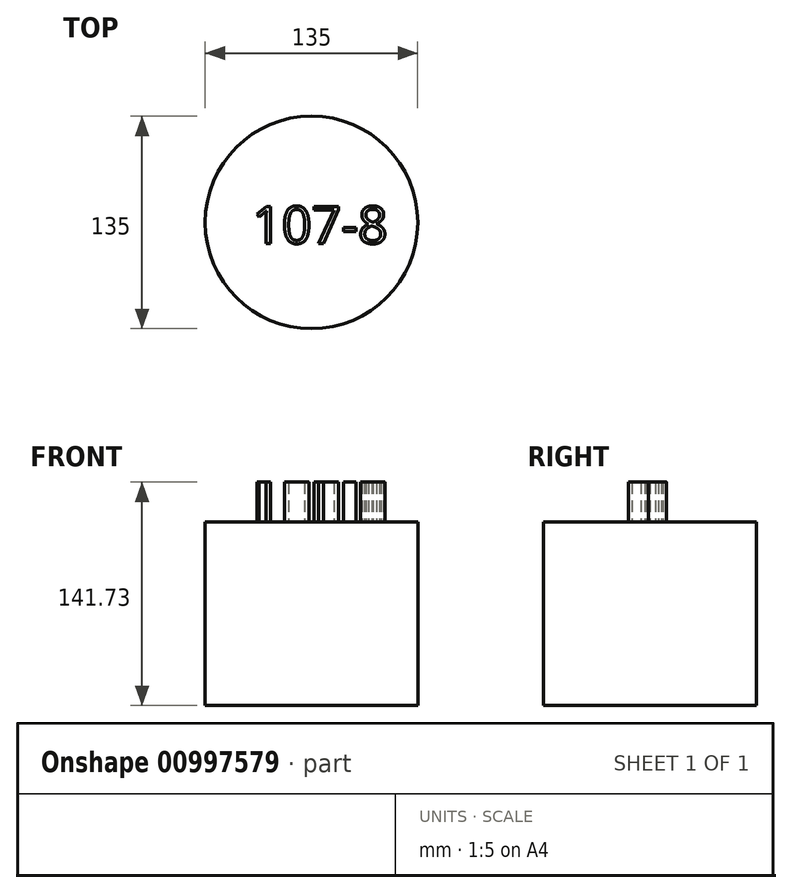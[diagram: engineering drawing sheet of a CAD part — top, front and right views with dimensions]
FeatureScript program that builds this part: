
annotation { "Feature Type Name" : "Feature", "Feature Type Description" : "" }
export const myFeature = defineFeature(function(context is Context, id is Id, definition is map)
    precondition{}
    {
        {
            var Q0;
            Q0=qCreatedBy(makeId("Top.planeOp"),FACE);
            var sketch = newSketch(context, id + "F0", { "sketchPlane" : qUnion([Q0])});
            skCircle(sketch, "E0", {"center": v(0, 0) * mm, "radius": 67.5 * mm});
            skSolve(sketch);
        }
        {
            var Q0;
            Q0=makeQuery(id+"F0.imprint","IMPRINT",FACE,{"disambiguationData":[TD([[makeQuery(id+"F0.imprint","IMPRINT",EDGE,{"derivedFrom":sQuery(id+"F0.wireOp",EDGE,"E0")}),1.0]])]});
            extrude(context, id + "F1", {"entities" : qUnion([Q0]), "depth" : 116.33 * mm, "offsetDistance" : 25.4 * mm});
        }
        {
            var Q0;
            Q0=makeQuery(id+"F1.opExtrude","CAP_FACE",FACE,{"disambiguationData":[OSD([sQuery(id+"F0.wireOp",EDGE,"E0")])],"isStart":false});
            var sketch = newSketch(context, id + "F2", { "sketchPlane" : qUnion([Q0])});
            skText(sketch, "E1", { "text": "107-8", "fontName": "OpenSans-Regular.ttf"});
            const initialGuessF2  = {"E1": [-0.03766, -0.01336, 1, 0, 0.02374]};
            skSetInitialGuess(sketch, initialGuessF2);
            skSolve(sketch);
        }
        {
            var Q0;
            Q0 = qSketchRegion(id + "F2", true);
            extrude(context, id + "F3", {"entities" : qUnion([Q0]), "operationType" : NewBodyOperationType.ADD, "depth" : 25.4 * mm, "offsetDistance" : 25.4 * mm});
        }
    });
